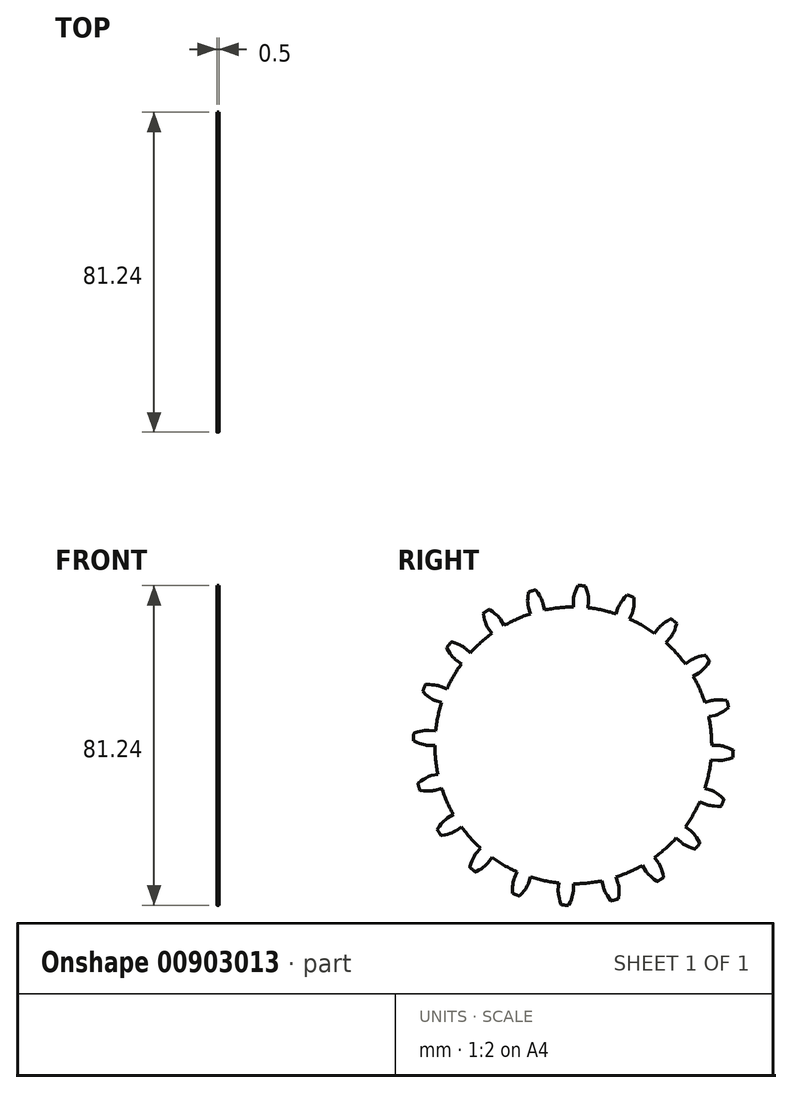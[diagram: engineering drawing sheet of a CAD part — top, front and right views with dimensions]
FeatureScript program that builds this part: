
annotation { "Feature Type Name" : "Feature", "Feature Type Description" : "" }
export const myFeature = defineFeature(function(context is Context, id is Id, definition is map)
    precondition{}
    {
        {
            assignVariable(context, id + "F0", {"name" : "GearThickness", "anyValue" : .5});
        }
        {
            var Q0;
            Q0=qCreatedBy(makeId("Right.planeOp"),FACE);
            var sketch = newSketch(context, id + "F1", { "sketchPlane" : qUnion([Q0])});
            skCircle(sketch, "E0", {"center": v(0, 0) * mm, "radius": 35.16 * mm});
            skCircle(sketch, "E1", {"center": v(0, 0) * mm, "radius": 36.89 * mm, "construction": true});
            skCircle(sketch, "E2", {"center": v(0, 0) * mm, "radius": 38.1 * mm, "construction": true});
            skCircle(sketch, "E3", {"center": v(0, 0) * mm, "radius": 40.64 * mm});
            skLineSegment(sketch, "E4", {"start": v(0, 0) * mm, "end": v(-36.89, 0) * mm, "construction": true});
            skLineSegment(sketch, "E5.1.0", {"start": v(0, 0) * mm, "end": v(-36.84, 1.84) * mm, "construction": true});
            skLineSegment(sketch, "E5.2.0", {"start": v(0, 0) * mm, "end": v(-36.7, 3.68) * mm, "construction": true});
            skLineSegment(sketch, "E5.3.0", {"start": v(0, 0) * mm, "end": v(-36.47, 5.51) * mm, "construction": true});
            skLineSegment(sketch, "E5.4.0", {"start": v(0, 0) * mm, "end": v(-36.15, 7.33) * mm, "construction": true});
            skLineSegment(sketch, "E5.5.0", {"start": v(0, 0) * mm, "end": v(-35.74, 9.13) * mm, "construction": true});
            skLineSegment(sketch, "E5.6.0", {"start": v(0, 0) * mm, "end": v(-35.24, 10.9) * mm, "construction": true});
            skLineSegment(sketch, "E5.7.0", {"start": v(0, 0) * mm, "end": v(-34.65, 12.65) * mm, "construction": true});
            skLineSegment(sketch, "E5.8.0", {"start": v(0, 0) * mm, "end": v(-33.97, 14.36) * mm, "construction": true});
            skLineSegment(sketch, "E5.9.0", {"start": v(0, 0) * mm, "end": v(-33.21, 16.04) * mm, "construction": true});
            skLineSegment(sketch, "E5.10.0", {"start": v(0, 0) * mm, "end": v(-32.37, 17.68) * mm, "construction": true});
            skLineSegment(sketch, "E5.11.0", {"start": v(0, 0) * mm, "end": v(-31.45, 19.28) * mm, "construction": true});
            skLineSegment(sketch, "E5.12.0", {"start": v(0, 0) * mm, "end": v(-30.44, 20.83) * mm, "construction": true});
            skLineSegment(sketch, "E5.13.0", {"start": v(0, 0) * mm, "end": v(-29.36, 22.32) * mm, "construction": true});
            skLineSegment(sketch, "E5.14.0", {"start": v(0, 0) * mm, "end": v(-28.21, 23.76) * mm, "construction": true});
            skLineSegment(sketch, "E5.anchor2", {"start": v(0, 0) * mm, "end": v(-28.21, 23.76) * mm, "construction": true});
            skLineSegment(sketch, "E6", {"start": v(-36.84, 1.84) * mm, "end": v(-36.93, 0) * mm, "construction": true});
            skLineSegment(sketch, "E7", {"start": v(-36.7, 3.68) * mm, "end": v(-37.07, 0.01) * mm, "construction": true});
            skLineSegment(sketch, "E8", {"start": v(-36.47, 5.51) * mm, "end": v(-37.3, 0.04) * mm, "construction": true});
            skLineSegment(sketch, "E9", {"start": v(-35.74, 9.13) * mm, "end": v(-38.02, 0.2) * mm, "construction": true});
            skLineSegment(sketch, "E10", {"start": v(-35.24, 10.9) * mm, "end": v(-38.5, 0.33) * mm, "construction": true});
            skLineSegment(sketch, "E11", {"start": v(-34.65, 12.65) * mm, "end": v(-39.08, 0.52) * mm, "construction": true});
            skLineSegment(sketch, "E12", {"start": v(-33.97, 14.36) * mm, "end": v(-39.72, 0.77) * mm, "construction": true});
            skLineSegment(sketch, "E13", {"start": v(-33.21, 16.04) * mm, "end": v(-40.43, 1.1) * mm, "construction": true});
            skLineSegment(sketch, "E14", {"start": v(-32.37, 17.68) * mm, "end": v(-41.21, 1.5) * mm, "construction": true});
            skLineSegment(sketch, "E15", {"start": v(-31.45, 19.28) * mm, "end": v(-42.05, 1.98) * mm, "construction": true});
            skLineSegment(sketch, "E16", {"start": v(-36.15, 7.33) * mm, "end": v(-37.62, 0.1) * mm, "construction": true});
            skLineSegment(sketch, "E17", {"start": v(-30.44, 20.83) * mm, "end": v(-42.94, 2.56) * mm, "construction": true});
            skLineSegment(sketch, "E18", {"start": v(-29.36, 22.32) * mm, "end": v(-43.87, 3.24) * mm, "construction": true});
            skLineSegment(sketch, "E19", {"start": v(-28.21, 23.76) * mm, "end": v(-44.85, 4.01) * mm, "construction": true});
            skLineSegment(sketch, "E20", {"start": v(0, 0) * mm, "end": v(-36.84, 1.93) * mm, "construction": true});
            skLineSegment(sketch, "E21", {"start": v(-35.16, 0) * mm, "end": v(-36.89, 0) * mm});
            skLineSegment(sketch, "E22.MirrorCS", {"start": v(-34.97, 3.68) * mm, "end": v(-36.68, 3.86) * mm});
            skLineSegment(sketch, "E23", {"start": v(-36.89, 0) * mm, "end": v(-36.93, 0) * mm});
            skLineSegment(sketch, "E24", {"start": v(-36.93, 0) * mm, "end": v(-37.07, 0.01) * mm});
            skLineSegment(sketch, "E25", {"start": v(-37.07, 0.01) * mm, "end": v(-37.3, 0.04) * mm});
            skLineSegment(sketch, "E26", {"start": v(-37.3, 0.04) * mm, "end": v(-37.62, 0.1) * mm});
            skLineSegment(sketch, "E27", {"start": v(-37.62, 0.1) * mm, "end": v(-38.02, 0.2) * mm});
            skLineSegment(sketch, "E28", {"start": v(-38.02, 0.2) * mm, "end": v(-38.5, 0.33) * mm});
            skLineSegment(sketch, "E29", {"start": v(-38.5, 0.33) * mm, "end": v(-39.08, 0.52) * mm});
            skLineSegment(sketch, "E30", {"start": v(-39.08, 0.52) * mm, "end": v(-39.72, 0.77) * mm});
            skLineSegment(sketch, "E31", {"start": v(-39.72, 0.77) * mm, "end": v(-40.43, 1.1) * mm});
            skLineSegment(sketch, "E32", {"start": v(-40.43, 1.1) * mm, "end": v(-41.21, 1.5) * mm});
            skLineSegment(sketch, "E33", {"start": v(-41.21, 1.5) * mm, "end": v(-42.05, 1.98) * mm});
            skLineSegment(sketch, "E34", {"start": v(-42.05, 1.98) * mm, "end": v(-42.94, 2.56) * mm});
            skLineSegment(sketch, "E35", {"start": v(-42.94, 2.56) * mm, "end": v(-43.87, 3.24) * mm});
            skLineSegment(sketch, "E36", {"start": v(-43.87, 3.24) * mm, "end": v(-44.85, 4.01) * mm});
            skLineSegment(sketch, "E37.MirrorCS", {"start": v(-36.68, 3.86) * mm, "end": v(-36.73, 3.86) * mm});
            skLineSegment(sketch, "E38.MirrorCS", {"start": v(-36.73, 3.86) * mm, "end": v(-36.87, 3.86) * mm});
            skLineSegment(sketch, "E39.MirrorCS", {"start": v(-36.87, 3.86) * mm, "end": v(-37.1, 3.86) * mm});
            skLineSegment(sketch, "E40.MirrorCS", {"start": v(-37.1, 3.86) * mm, "end": v(-37.42, 3.83) * mm});
            skLineSegment(sketch, "E41.MirrorCS", {"start": v(-37.83, 3.78) * mm, "end": v(-38.33, 3.7) * mm});
            skLineSegment(sketch, "E42.MirrorCS", {"start": v(-38.33, 3.7) * mm, "end": v(-38.92, 3.57) * mm});
            skLineSegment(sketch, "E43.MirrorCS", {"start": v(-38.92, 3.57) * mm, "end": v(-39.58, 3.38) * mm});
            skLineSegment(sketch, "E44.MirrorCS", {"start": v(-39.58, 3.38) * mm, "end": v(-40.33, 3.13) * mm});
            skLineSegment(sketch, "E45.MirrorCS", {"start": v(-41.14, 2.82) * mm, "end": v(-42.03, 2.42) * mm});
            skLineSegment(sketch, "E46.MirrorCS", {"start": v(-40.33, 3.13) * mm, "end": v(-41.14, 2.82) * mm});
            skLineSegment(sketch, "E47.MirrorCS", {"start": v(-42.03, 2.42) * mm, "end": v(-42.97, 1.94) * mm});
            skLineSegment(sketch, "E48.MirrorCS", {"start": v(-42.97, 1.94) * mm, "end": v(-43.97, 1.37) * mm});
            skLineSegment(sketch, "E49.MirrorCS", {"start": v(-43.97, 1.37) * mm, "end": v(-45.02, 0.7) * mm});
            skLineSegment(sketch, "E50.MirrorCS", {"start": v(-37.42, 3.83) * mm, "end": v(-37.83, 3.78) * mm});
            skLineSegment(sketch, "E51.1.0", {"start": v(-33.44, -10.87) * mm, "end": v(-35.08, -11.4) * mm});
            skLineSegment(sketch, "E51.1.1", {"start": v(-40.72, -10.68) * mm, "end": v(-41.47, -11.43) * mm});
            skLineSegment(sketch, "E51.1.2", {"start": v(-34.4, -7.31) * mm, "end": v(-36.08, -7.67) * mm});
            skLineSegment(sketch, "E51.1.3", {"start": v(-40, -10.03) * mm, "end": v(-40.72, -10.68) * mm});
            skLineSegment(sketch, "E51.1.4", {"start": v(-39.66, -11.31) * mm, "end": v(-40.6, -11.1) * mm});
            skLineSegment(sketch, "E51.1.5", {"start": v(-40.6, -11.1) * mm, "end": v(-41.63, -10.83) * mm});
            skLineSegment(sketch, "E51.1.6", {"start": v(-39.32, -9.48) * mm, "end": v(-40, -10.03) * mm});
            skLineSegment(sketch, "E51.1.7", {"start": v(-42.24, -12.29) * mm, "end": v(-43.03, -13.25) * mm});
            skLineSegment(sketch, "E51.1.8", {"start": v(-38.7, -9.02) * mm, "end": v(-39.32, -9.48) * mm});
            skLineSegment(sketch, "E51.1.9", {"start": v(-42.73, -10.48) * mm, "end": v(-43.9, -10.04) * mm});
            skLineSegment(sketch, "E51.1.10", {"start": v(-41.47, -11.43) * mm, "end": v(-42.24, -12.29) * mm});
            skLineSegment(sketch, "E51.1.11", {"start": v(-38.8, -11.45) * mm, "end": v(-39.66, -11.31) * mm});
            skLineSegment(sketch, "E51.1.12", {"start": v(-41.63, -10.83) * mm, "end": v(-42.73, -10.48) * mm});
            skLineSegment(sketch, "E51.1.13", {"start": v(-37.15, -8.1) * mm, "end": v(-37.6, -8.33) * mm});
            skLineSegment(sketch, "E51.1.14", {"start": v(-37.6, -8.33) * mm, "end": v(-38.11, -8.63) * mm});
            skLineSegment(sketch, "E51.1.15", {"start": v(-38.11, -8.63) * mm, "end": v(-38.7, -9.02) * mm});
            skLineSegment(sketch, "E51.1.16", {"start": v(-37.33, -11.58) * mm, "end": v(-38.02, -11.54) * mm});
            skLineSegment(sketch, "E51.1.17", {"start": v(-36.73, -11.59) * mm, "end": v(-37.33, -11.58) * mm});
            skLineSegment(sketch, "E51.1.18", {"start": v(-38.02, -11.54) * mm, "end": v(-38.8, -11.45) * mm});
            skLineSegment(sketch, "E51.1.19", {"start": v(-36.77, -7.92) * mm, "end": v(-37.15, -8.1) * mm});
            skLineSegment(sketch, "E51.1.20", {"start": v(-36.48, -7.8) * mm, "end": v(-36.77, -7.92) * mm});
            skLineSegment(sketch, "E51.1.21", {"start": v(-36.22, -11.57) * mm, "end": v(-36.73, -11.59) * mm});
            skLineSegment(sketch, "E51.1.22", {"start": v(-35.8, -11.53) * mm, "end": v(-36.22, -11.57) * mm});
            skLineSegment(sketch, "E51.1.23", {"start": v(-35.26, -11.44) * mm, "end": v(-35.49, -11.49) * mm});
            skLineSegment(sketch, "E51.1.24", {"start": v(-36.08, -7.67) * mm, "end": v(-36.13, -7.68) * mm});
            skLineSegment(sketch, "E51.1.25", {"start": v(-36.13, -7.68) * mm, "end": v(-36.26, -7.72) * mm});
            skLineSegment(sketch, "E51.1.26", {"start": v(-35.49, -11.49) * mm, "end": v(-35.8, -11.53) * mm});
            skLineSegment(sketch, "E51.1.27", {"start": v(-36.26, -7.72) * mm, "end": v(-36.48, -7.8) * mm});
            skLineSegment(sketch, "E51.1.28", {"start": v(-35.13, -11.41) * mm, "end": v(-35.26, -11.44) * mm});
            skLineSegment(sketch, "E51.1.29", {"start": v(-35.08, -11.4) * mm, "end": v(-35.13, -11.41) * mm});
            skLineSegment(sketch, "E51.2.0", {"start": v(-28.45, -20.67) * mm, "end": v(-29.84, -21.68) * mm});
            skLineSegment(sketch, "E51.2.1", {"start": v(-35.42, -22.74) * mm, "end": v(-35.9, -23.69) * mm});
            skLineSegment(sketch, "E51.2.2", {"start": v(-30.45, -17.58) * mm, "end": v(-31.94, -18.44) * mm});
            skLineSegment(sketch, "E51.2.3", {"start": v(-34.94, -21.9) * mm, "end": v(-35.42, -22.74) * mm});
            skLineSegment(sketch, "E51.2.4", {"start": v(-34.22, -23.01) * mm, "end": v(-35.19, -23.11) * mm});
            skLineSegment(sketch, "E51.2.5", {"start": v(-35.19, -23.11) * mm, "end": v(-36.24, -23.17) * mm});
            skLineSegment(sketch, "E51.2.6", {"start": v(-34.47, -21.17) * mm, "end": v(-34.94, -21.9) * mm});
            skLineSegment(sketch, "E51.2.7", {"start": v(-36.38, -24.74) * mm, "end": v(-36.83, -25.9) * mm});
            skLineSegment(sketch, "E51.2.8", {"start": v(-34.01, -20.53) * mm, "end": v(-34.47, -21.17) * mm});
            skLineSegment(sketch, "E51.2.9", {"start": v(-37.4, -23.17) * mm, "end": v(-38.64, -23.11) * mm});
            skLineSegment(sketch, "E51.2.10", {"start": v(-35.9, -23.69) * mm, "end": v(-36.38, -24.74) * mm});
            skLineSegment(sketch, "E51.2.11", {"start": v(-33.36, -22.88) * mm, "end": v(-34.22, -23.01) * mm});
            skLineSegment(sketch, "E51.2.12", {"start": v(-36.24, -23.17) * mm, "end": v(-37.4, -23.17) * mm});
            skLineSegment(sketch, "E51.2.13", {"start": v(-32.83, -19.18) * mm, "end": v(-33.19, -19.54) * mm});
            skLineSegment(sketch, "E51.2.14", {"start": v(-33.19, -19.54) * mm, "end": v(-33.58, -19.99) * mm});
            skLineSegment(sketch, "E51.2.15", {"start": v(-33.58, -19.99) * mm, "end": v(-34.01, -20.53) * mm});
            skLineSegment(sketch, "E51.2.16", {"start": v(-31.92, -22.55) * mm, "end": v(-32.59, -22.72) * mm});
            skLineSegment(sketch, "E51.2.17", {"start": v(-31.35, -22.37) * mm, "end": v(-31.92, -22.55) * mm});
            skLineSegment(sketch, "E51.2.18", {"start": v(-32.59, -22.72) * mm, "end": v(-33.36, -22.88) * mm});
            skLineSegment(sketch, "E51.2.19", {"start": v(-32.53, -18.9) * mm, "end": v(-32.83, -19.18) * mm});
            skLineSegment(sketch, "E51.2.20", {"start": v(-32.28, -18.69) * mm, "end": v(-32.53, -18.9) * mm});
            skLineSegment(sketch, "E51.2.21", {"start": v(-30.87, -22.2) * mm, "end": v(-31.35, -22.37) * mm});
            skLineSegment(sketch, "E51.2.22", {"start": v(-30.5, -22.03) * mm, "end": v(-30.87, -22.2) * mm});
            skLineSegment(sketch, "E51.2.23", {"start": v(-30, -21.78) * mm, "end": v(-30.2, -21.9) * mm});
            skLineSegment(sketch, "E51.2.24", {"start": v(-31.94, -18.44) * mm, "end": v(-31.98, -18.47) * mm});
            skLineSegment(sketch, "E51.2.25", {"start": v(-31.98, -18.47) * mm, "end": v(-32.1, -18.55) * mm});
            skLineSegment(sketch, "E51.2.26", {"start": v(-30.2, -21.9) * mm, "end": v(-30.5, -22.03) * mm});
            skLineSegment(sketch, "E51.2.27", {"start": v(-32.1, -18.55) * mm, "end": v(-32.28, -18.69) * mm});
            skLineSegment(sketch, "E51.2.28", {"start": v(-29.88, -21.7) * mm, "end": v(-30, -21.78) * mm});
            skLineSegment(sketch, "E51.2.29", {"start": v(-29.84, -21.68) * mm, "end": v(-29.88, -21.7) * mm});
            skLineSegment(sketch, "E51.3.0", {"start": v(-20.67, -28.45) * mm, "end": v(-21.68, -29.84) * mm});
            skLineSegment(sketch, "E51.3.1", {"start": v(-26.66, -32.58) * mm, "end": v(-26.83, -33.62) * mm});
            skLineSegment(sketch, "E51.3.2", {"start": v(-23.53, -26.13) * mm, "end": v(-24.68, -27.41) * mm});
            skLineSegment(sketch, "E51.3.3", {"start": v(-26.46, -31.63) * mm, "end": v(-26.66, -32.58) * mm});
            skLineSegment(sketch, "E51.3.4", {"start": v(-25.44, -32.46) * mm, "end": v(-26.32, -32.85) * mm});
            skLineSegment(sketch, "E51.3.5", {"start": v(-26.32, -32.85) * mm, "end": v(-27.31, -33.23) * mm});
            skLineSegment(sketch, "E51.3.6", {"start": v(-26.24, -30.78) * mm, "end": v(-26.46, -31.63) * mm});
            skLineSegment(sketch, "E51.3.7", {"start": v(-26.95, -34.77) * mm, "end": v(-27.02, -36.01) * mm});
            skLineSegment(sketch, "E51.3.8", {"start": v(-26, -30.04) * mm, "end": v(-26.24, -30.78) * mm});
            skLineSegment(sketch, "E51.3.9", {"start": v(-28.4, -33.6) * mm, "end": v(-29.6, -33.92) * mm});
            skLineSegment(sketch, "E51.3.10", {"start": v(-26.83, -33.62) * mm, "end": v(-26.95, -34.77) * mm});
            skLineSegment(sketch, "E51.3.11", {"start": v(-24.65, -32.07) * mm, "end": v(-25.44, -32.46) * mm});
            skLineSegment(sketch, "E51.3.12", {"start": v(-27.31, -33.23) * mm, "end": v(-28.4, -33.6) * mm});
            skLineSegment(sketch, "E51.3.13", {"start": v(-25.3, -28.38) * mm, "end": v(-25.52, -28.84) * mm});
            skLineSegment(sketch, "E51.3.14", {"start": v(-25.52, -28.84) * mm, "end": v(-25.76, -29.39) * mm});
            skLineSegment(sketch, "E51.3.15", {"start": v(-25.76, -29.39) * mm, "end": v(-26, -30.04) * mm});
            skLineSegment(sketch, "E51.3.16", {"start": v(-23.4, -31.3) * mm, "end": v(-23.97, -31.68) * mm});
            skLineSegment(sketch, "E51.3.17", {"start": v(-22.9, -30.96) * mm, "end": v(-23.4, -31.3) * mm});
            skLineSegment(sketch, "E51.3.18", {"start": v(-23.97, -31.68) * mm, "end": v(-24.65, -32.07) * mm});
            skLineSegment(sketch, "E51.3.19", {"start": v(-25.1, -28.02) * mm, "end": v(-25.3, -28.38) * mm});
            skLineSegment(sketch, "E51.3.20", {"start": v(-24.93, -27.75) * mm, "end": v(-25.1, -28.02) * mm});
            skLineSegment(sketch, "E51.3.21", {"start": v(-22.5, -30.65) * mm, "end": v(-22.9, -30.96) * mm});
            skLineSegment(sketch, "E51.3.22", {"start": v(-22.19, -30.38) * mm, "end": v(-22.5, -30.65) * mm});
            skLineSegment(sketch, "E51.3.23", {"start": v(-21.8, -29.98) * mm, "end": v(-21.96, -30.15) * mm});
            skLineSegment(sketch, "E51.3.24", {"start": v(-24.68, -27.41) * mm, "end": v(-24.71, -27.45) * mm});
            skLineSegment(sketch, "E51.3.25", {"start": v(-24.71, -27.45) * mm, "end": v(-24.8, -27.56) * mm});
            skLineSegment(sketch, "E51.3.26", {"start": v(-21.96, -30.15) * mm, "end": v(-22.19, -30.38) * mm});
            skLineSegment(sketch, "E51.3.27", {"start": v(-24.8, -27.56) * mm, "end": v(-24.93, -27.75) * mm});
            skLineSegment(sketch, "E51.3.28", {"start": v(-21.7, -29.88) * mm, "end": v(-21.8, -29.98) * mm});
            skLineSegment(sketch, "E51.3.29", {"start": v(-21.68, -29.84) * mm, "end": v(-21.7, -29.88) * mm});
            skLineSegment(sketch, "E51.4.0", {"start": v(-10.87, -33.44) * mm, "end": v(-11.4, -35.08) * mm});
            skLineSegment(sketch, "E51.4.1", {"start": v(-15.3, -39.22) * mm, "end": v(-15.13, -40.27) * mm});
            skLineSegment(sketch, "E51.4.2", {"start": v(-14.3, -32.12) * mm, "end": v(-15, -33.7) * mm});
            skLineSegment(sketch, "E51.4.3", {"start": v(-15.4, -38.26) * mm, "end": v(-15.3, -39.22) * mm});
            skLineSegment(sketch, "E51.4.4", {"start": v(-14.16, -38.73) * mm, "end": v(-14.88, -39.38) * mm});
            skLineSegment(sketch, "E51.4.5", {"start": v(-14.88, -39.38) * mm, "end": v(-15.7, -40.05) * mm});
            skLineSegment(sketch, "E51.4.6", {"start": v(-15.44, -37.39) * mm, "end": v(-15.4, -38.26) * mm});
            skLineSegment(sketch, "E51.4.7", {"start": v(-14.89, -41.4) * mm, "end": v(-14.57, -42.6) * mm});
            skLineSegment(sketch, "E51.4.8", {"start": v(-15.45, -36.6) * mm, "end": v(-15.44, -37.39) * mm});
            skLineSegment(sketch, "E51.4.9", {"start": v(-16.64, -40.73) * mm, "end": v(-17.68, -41.41) * mm});
            skLineSegment(sketch, "E51.4.10", {"start": v(-15.13, -40.27) * mm, "end": v(-14.89, -41.4) * mm});
            skLineSegment(sketch, "E51.4.11", {"start": v(-13.54, -38.12) * mm, "end": v(-14.16, -38.73) * mm});
            skLineSegment(sketch, "E51.4.12", {"start": v(-15.7, -40.05) * mm, "end": v(-16.64, -40.73) * mm});
            skLineSegment(sketch, "E51.4.13", {"start": v(-15.3, -34.81) * mm, "end": v(-15.36, -35.31) * mm});
            skLineSegment(sketch, "E51.4.14", {"start": v(-15.36, -35.31) * mm, "end": v(-15.42, -35.91) * mm});
            skLineSegment(sketch, "E51.4.15", {"start": v(-15.42, -35.91) * mm, "end": v(-15.45, -36.6) * mm});
            skLineSegment(sketch, "E51.4.16", {"start": v(-12.57, -37) * mm, "end": v(-13.01, -37.54) * mm});
            skLineSegment(sketch, "E51.4.17", {"start": v(-12.21, -36.52) * mm, "end": v(-12.57, -37) * mm});
            skLineSegment(sketch, "E51.4.18", {"start": v(-13.01, -37.54) * mm, "end": v(-13.54, -38.12) * mm});
            skLineSegment(sketch, "E51.4.19", {"start": v(-15.21, -34.4) * mm, "end": v(-15.3, -34.81) * mm});
            skLineSegment(sketch, "E51.4.20", {"start": v(-15.13, -34.1) * mm, "end": v(-15.21, -34.4) * mm});
            skLineSegment(sketch, "E51.4.21", {"start": v(-11.93, -36.1) * mm, "end": v(-12.21, -36.52) * mm});
            skLineSegment(sketch, "E51.4.22", {"start": v(-11.72, -35.75) * mm, "end": v(-11.93, -36.1) * mm});
            skLineSegment(sketch, "E51.4.23", {"start": v(-11.47, -35.25) * mm, "end": v(-11.57, -35.46) * mm});
            skLineSegment(sketch, "E51.4.24", {"start": v(-15, -33.7) * mm, "end": v(-15.02, -33.74) * mm});
            skLineSegment(sketch, "E51.4.25", {"start": v(-15.02, -33.74) * mm, "end": v(-15.07, -33.87) * mm});
            skLineSegment(sketch, "E51.4.26", {"start": v(-11.57, -35.46) * mm, "end": v(-11.72, -35.75) * mm});
            skLineSegment(sketch, "E51.4.27", {"start": v(-15.07, -33.87) * mm, "end": v(-15.13, -34.1) * mm});
            skLineSegment(sketch, "E51.4.28", {"start": v(-11.41, -35.12) * mm, "end": v(-11.47, -35.25) * mm});
            skLineSegment(sketch, "E51.4.29", {"start": v(-11.4, -35.08) * mm, "end": v(-11.41, -35.12) * mm});
            skLineSegment(sketch, "E51.5.0", {"start": v(0, -35.16) * mm, "end": v(0, -36.89) * mm});
            skLineSegment(sketch, "E51.5.1", {"start": v(-2.42, -42.03) * mm, "end": v(-1.94, -42.97) * mm});
            skLineSegment(sketch, "E51.5.2", {"start": v(-3.68, -34.97) * mm, "end": v(-3.86, -36.68) * mm});
            skLineSegment(sketch, "E51.5.3", {"start": v(-2.82, -41.14) * mm, "end": v(-2.42, -42.03) * mm});
            skLineSegment(sketch, "E51.5.4", {"start": v(-1.5, -41.21) * mm, "end": v(-1.98, -42.05) * mm});
            skLineSegment(sketch, "E51.5.5", {"start": v(-1.98, -42.05) * mm, "end": v(-2.56, -42.94) * mm});
            skLineSegment(sketch, "E51.5.6", {"start": v(-3.13, -40.33) * mm, "end": v(-2.82, -41.14) * mm});
            skLineSegment(sketch, "E51.5.7", {"start": v(-1.37, -43.97) * mm, "end": v(-0.7, -45.02) * mm});
            skLineSegment(sketch, "E51.5.8", {"start": v(-3.38, -39.58) * mm, "end": v(-3.13, -40.33) * mm});
            skLineSegment(sketch, "E51.5.9", {"start": v(-3.24, -43.87) * mm, "end": v(-4.01, -44.85) * mm});
            skLineSegment(sketch, "E51.5.10", {"start": v(-1.94, -42.97) * mm, "end": v(-1.37, -43.97) * mm});
            skLineSegment(sketch, "E51.5.11", {"start": v(-1.1, -40.43) * mm, "end": v(-1.5, -41.21) * mm});
            skLineSegment(sketch, "E51.5.12", {"start": v(-2.56, -42.94) * mm, "end": v(-3.24, -43.87) * mm});
            skLineSegment(sketch, "E51.5.13", {"start": v(-3.78, -37.83) * mm, "end": v(-3.7, -38.33) * mm});
            skLineSegment(sketch, "E51.5.14", {"start": v(-3.7, -38.33) * mm, "end": v(-3.57, -38.92) * mm});
            skLineSegment(sketch, "E51.5.15", {"start": v(-3.57, -38.92) * mm, "end": v(-3.38, -39.58) * mm});
            skLineSegment(sketch, "E51.5.16", {"start": v(-0.52, -39.08) * mm, "end": v(-0.77, -39.72) * mm});
            skLineSegment(sketch, "E51.5.17", {"start": v(-0.33, -38.5) * mm, "end": v(-0.52, -39.08) * mm});
            skLineSegment(sketch, "E51.5.18", {"start": v(-0.77, -39.72) * mm, "end": v(-1.1, -40.43) * mm});
            skLineSegment(sketch, "E51.5.19", {"start": v(-3.83, -37.42) * mm, "end": v(-3.78, -37.83) * mm});
            skLineSegment(sketch, "E51.5.20", {"start": v(-3.86, -37.1) * mm, "end": v(-3.83, -37.42) * mm});
            skLineSegment(sketch, "E51.5.21", {"start": v(-0.2, -38.02) * mm, "end": v(-0.33, -38.5) * mm});
            skLineSegment(sketch, "E51.5.22", {"start": v(-0.1, -37.62) * mm, "end": v(-0.2, -38.02) * mm});
            skLineSegment(sketch, "E51.5.23", {"start": v(-0.01, -37.07) * mm, "end": v(-0.04, -37.3) * mm});
            skLineSegment(sketch, "E51.5.24", {"start": v(-3.86, -36.68) * mm, "end": v(-3.86, -36.73) * mm});
            skLineSegment(sketch, "E51.5.25", {"start": v(-3.86, -36.73) * mm, "end": v(-3.86, -36.87) * mm});
            skLineSegment(sketch, "E51.5.26", {"start": v(-0.04, -37.3) * mm, "end": v(-0.1, -37.62) * mm});
            skLineSegment(sketch, "E51.5.27", {"start": v(-3.86, -36.87) * mm, "end": v(-3.86, -37.1) * mm});
            skLineSegment(sketch, "E51.5.28", {"start": v(0, -36.93) * mm, "end": v(-0.01, -37.07) * mm});
            skLineSegment(sketch, "E51.5.29", {"start": v(0, -36.89) * mm, "end": v(0, -36.93) * mm});
            skLineSegment(sketch, "E51.6.0", {"start": v(10.87, -33.44) * mm, "end": v(11.4, -35.08) * mm});
            skLineSegment(sketch, "E51.6.1", {"start": v(10.68, -40.72) * mm, "end": v(11.43, -41.47) * mm});
            skLineSegment(sketch, "E51.6.2", {"start": v(7.31, -34.4) * mm, "end": v(7.67, -36.08) * mm});
            skLineSegment(sketch, "E51.6.3", {"start": v(10.03, -40) * mm, "end": v(10.68, -40.72) * mm});
            skLineSegment(sketch, "E51.6.4", {"start": v(11.31, -39.66) * mm, "end": v(11.1, -40.6) * mm});
            skLineSegment(sketch, "E51.6.5", {"start": v(11.1, -40.6) * mm, "end": v(10.83, -41.63) * mm});
            skLineSegment(sketch, "E51.6.6", {"start": v(9.48, -39.32) * mm, "end": v(10.03, -40) * mm});
            skLineSegment(sketch, "E51.6.7", {"start": v(12.29, -42.24) * mm, "end": v(13.25, -43.03) * mm});
            skLineSegment(sketch, "E51.6.8", {"start": v(9.02, -38.7) * mm, "end": v(9.48, -39.32) * mm});
            skLineSegment(sketch, "E51.6.9", {"start": v(10.48, -42.73) * mm, "end": v(10.04, -43.9) * mm});
            skLineSegment(sketch, "E51.6.10", {"start": v(11.43, -41.47) * mm, "end": v(12.29, -42.24) * mm});
            skLineSegment(sketch, "E51.6.11", {"start": v(11.45, -38.8) * mm, "end": v(11.31, -39.66) * mm});
            skLineSegment(sketch, "E51.6.12", {"start": v(10.83, -41.63) * mm, "end": v(10.48, -42.73) * mm});
            skLineSegment(sketch, "E51.6.13", {"start": v(8.1, -37.15) * mm, "end": v(8.33, -37.6) * mm});
            skLineSegment(sketch, "E51.6.14", {"start": v(8.33, -37.6) * mm, "end": v(8.63, -38.11) * mm});
            skLineSegment(sketch, "E51.6.15", {"start": v(8.63, -38.11) * mm, "end": v(9.02, -38.7) * mm});
            skLineSegment(sketch, "E51.6.16", {"start": v(11.58, -37.33) * mm, "end": v(11.54, -38.02) * mm});
            skLineSegment(sketch, "E51.6.17", {"start": v(11.59, -36.73) * mm, "end": v(11.58, -37.33) * mm});
            skLineSegment(sketch, "E51.6.18", {"start": v(11.54, -38.02) * mm, "end": v(11.45, -38.8) * mm});
            skLineSegment(sketch, "E51.6.19", {"start": v(7.92, -36.77) * mm, "end": v(8.1, -37.15) * mm});
            skLineSegment(sketch, "E51.6.20", {"start": v(7.8, -36.48) * mm, "end": v(7.92, -36.77) * mm});
            skLineSegment(sketch, "E51.6.21", {"start": v(11.57, -36.22) * mm, "end": v(11.59, -36.73) * mm});
            skLineSegment(sketch, "E51.6.22", {"start": v(11.53, -35.8) * mm, "end": v(11.57, -36.22) * mm});
            skLineSegment(sketch, "E51.6.23", {"start": v(11.44, -35.26) * mm, "end": v(11.49, -35.49) * mm});
            skLineSegment(sketch, "E51.6.24", {"start": v(7.67, -36.08) * mm, "end": v(7.68, -36.13) * mm});
            skLineSegment(sketch, "E51.6.25", {"start": v(7.68, -36.13) * mm, "end": v(7.72, -36.26) * mm});
            skLineSegment(sketch, "E51.6.26", {"start": v(11.49, -35.49) * mm, "end": v(11.53, -35.8) * mm});
            skLineSegment(sketch, "E51.6.27", {"start": v(7.72, -36.26) * mm, "end": v(7.8, -36.48) * mm});
            skLineSegment(sketch, "E51.6.28", {"start": v(11.41, -35.13) * mm, "end": v(11.44, -35.26) * mm});
            skLineSegment(sketch, "E51.6.29", {"start": v(11.4, -35.08) * mm, "end": v(11.41, -35.13) * mm});
            skLineSegment(sketch, "E51.7.0", {"start": v(20.67, -28.45) * mm, "end": v(21.68, -29.84) * mm});
            skLineSegment(sketch, "E51.7.1", {"start": v(22.74, -35.42) * mm, "end": v(23.69, -35.9) * mm});
            skLineSegment(sketch, "E51.7.2", {"start": v(17.58, -30.45) * mm, "end": v(18.44, -31.94) * mm});
            skLineSegment(sketch, "E51.7.3", {"start": v(21.9, -34.94) * mm, "end": v(22.74, -35.42) * mm});
            skLineSegment(sketch, "E51.7.4", {"start": v(23.01, -34.22) * mm, "end": v(23.11, -35.19) * mm});
            skLineSegment(sketch, "E51.7.5", {"start": v(23.11, -35.19) * mm, "end": v(23.17, -36.24) * mm});
            skLineSegment(sketch, "E51.7.6", {"start": v(21.17, -34.47) * mm, "end": v(21.9, -34.94) * mm});
            skLineSegment(sketch, "E51.7.7", {"start": v(24.74, -36.38) * mm, "end": v(25.9, -36.83) * mm});
            skLineSegment(sketch, "E51.7.8", {"start": v(20.53, -34.01) * mm, "end": v(21.17, -34.47) * mm});
            skLineSegment(sketch, "E51.7.9", {"start": v(23.17, -37.4) * mm, "end": v(23.11, -38.64) * mm});
            skLineSegment(sketch, "E51.7.10", {"start": v(23.69, -35.9) * mm, "end": v(24.74, -36.38) * mm});
            skLineSegment(sketch, "E51.7.11", {"start": v(22.88, -33.36) * mm, "end": v(23.01, -34.22) * mm});
            skLineSegment(sketch, "E51.7.12", {"start": v(23.17, -36.24) * mm, "end": v(23.17, -37.4) * mm});
            skLineSegment(sketch, "E51.7.13", {"start": v(19.18, -32.83) * mm, "end": v(19.54, -33.19) * mm});
            skLineSegment(sketch, "E51.7.14", {"start": v(19.54, -33.19) * mm, "end": v(19.99, -33.58) * mm});
            skLineSegment(sketch, "E51.7.15", {"start": v(19.99, -33.58) * mm, "end": v(20.53, -34.01) * mm});
            skLineSegment(sketch, "E51.7.16", {"start": v(22.55, -31.92) * mm, "end": v(22.72, -32.59) * mm});
            skLineSegment(sketch, "E51.7.17", {"start": v(22.37, -31.35) * mm, "end": v(22.55, -31.92) * mm});
            skLineSegment(sketch, "E51.7.18", {"start": v(22.72, -32.59) * mm, "end": v(22.88, -33.36) * mm});
            skLineSegment(sketch, "E51.7.19", {"start": v(18.9, -32.53) * mm, "end": v(19.18, -32.83) * mm});
            skLineSegment(sketch, "E51.7.20", {"start": v(18.69, -32.28) * mm, "end": v(18.9, -32.53) * mm});
            skLineSegment(sketch, "E51.7.21", {"start": v(22.2, -30.87) * mm, "end": v(22.37, -31.35) * mm});
            skLineSegment(sketch, "E51.7.22", {"start": v(22.03, -30.5) * mm, "end": v(22.2, -30.87) * mm});
            skLineSegment(sketch, "E51.7.23", {"start": v(21.78, -30) * mm, "end": v(21.9, -30.2) * mm});
            skLineSegment(sketch, "E51.7.24", {"start": v(18.44, -31.94) * mm, "end": v(18.47, -31.98) * mm});
            skLineSegment(sketch, "E51.7.25", {"start": v(18.47, -31.98) * mm, "end": v(18.55, -32.1) * mm});
            skLineSegment(sketch, "E51.7.26", {"start": v(21.9, -30.2) * mm, "end": v(22.03, -30.5) * mm});
            skLineSegment(sketch, "E51.7.27", {"start": v(18.55, -32.1) * mm, "end": v(18.69, -32.28) * mm});
            skLineSegment(sketch, "E51.7.28", {"start": v(21.7, -29.88) * mm, "end": v(21.78, -30) * mm});
            skLineSegment(sketch, "E51.7.29", {"start": v(21.68, -29.84) * mm, "end": v(21.7, -29.88) * mm});
            skLineSegment(sketch, "E51.8.0", {"start": v(28.45, -20.67) * mm, "end": v(29.84, -21.68) * mm});
            skLineSegment(sketch, "E51.8.1", {"start": v(32.58, -26.66) * mm, "end": v(33.62, -26.83) * mm});
            skLineSegment(sketch, "E51.8.2", {"start": v(26.13, -23.53) * mm, "end": v(27.41, -24.68) * mm});
            skLineSegment(sketch, "E51.8.3", {"start": v(31.63, -26.46) * mm, "end": v(32.58, -26.66) * mm});
            skLineSegment(sketch, "E51.8.4", {"start": v(32.46, -25.44) * mm, "end": v(32.85, -26.32) * mm});
            skLineSegment(sketch, "E51.8.5", {"start": v(32.85, -26.32) * mm, "end": v(33.23, -27.31) * mm});
            skLineSegment(sketch, "E51.8.6", {"start": v(30.78, -26.24) * mm, "end": v(31.63, -26.46) * mm});
            skLineSegment(sketch, "E51.8.7", {"start": v(34.77, -26.95) * mm, "end": v(36.01, -27.02) * mm});
            skLineSegment(sketch, "E51.8.8", {"start": v(30.04, -26) * mm, "end": v(30.78, -26.24) * mm});
            skLineSegment(sketch, "E51.8.9", {"start": v(33.6, -28.4) * mm, "end": v(33.92, -29.6) * mm});
            skLineSegment(sketch, "E51.8.10", {"start": v(33.62, -26.83) * mm, "end": v(34.77, -26.95) * mm});
            skLineSegment(sketch, "E51.8.11", {"start": v(32.07, -24.65) * mm, "end": v(32.46, -25.44) * mm});
            skLineSegment(sketch, "E51.8.12", {"start": v(33.23, -27.31) * mm, "end": v(33.6, -28.4) * mm});
            skLineSegment(sketch, "E51.8.13", {"start": v(28.38, -25.3) * mm, "end": v(28.84, -25.52) * mm});
            skLineSegment(sketch, "E51.8.14", {"start": v(28.84, -25.52) * mm, "end": v(29.39, -25.76) * mm});
            skLineSegment(sketch, "E51.8.15", {"start": v(29.39, -25.76) * mm, "end": v(30.04, -26) * mm});
            skLineSegment(sketch, "E51.8.16", {"start": v(31.3, -23.4) * mm, "end": v(31.68, -23.97) * mm});
            skLineSegment(sketch, "E51.8.17", {"start": v(30.96, -22.9) * mm, "end": v(31.3, -23.4) * mm});
            skLineSegment(sketch, "E51.8.18", {"start": v(31.68, -23.97) * mm, "end": v(32.07, -24.65) * mm});
            skLineSegment(sketch, "E51.8.19", {"start": v(28.02, -25.1) * mm, "end": v(28.38, -25.3) * mm});
            skLineSegment(sketch, "E51.8.20", {"start": v(27.75, -24.93) * mm, "end": v(28.02, -25.1) * mm});
            skLineSegment(sketch, "E51.8.21", {"start": v(30.65, -22.5) * mm, "end": v(30.96, -22.9) * mm});
            skLineSegment(sketch, "E51.8.22", {"start": v(30.38, -22.19) * mm, "end": v(30.65, -22.5) * mm});
            skLineSegment(sketch, "E51.8.23", {"start": v(29.98, -21.8) * mm, "end": v(30.15, -21.96) * mm});
            skLineSegment(sketch, "E51.8.24", {"start": v(27.41, -24.68) * mm, "end": v(27.45, -24.71) * mm});
            skLineSegment(sketch, "E51.8.25", {"start": v(27.45, -24.71) * mm, "end": v(27.56, -24.8) * mm});
            skLineSegment(sketch, "E51.8.26", {"start": v(30.15, -21.96) * mm, "end": v(30.38, -22.19) * mm});
            skLineSegment(sketch, "E51.8.27", {"start": v(27.56, -24.8) * mm, "end": v(27.75, -24.93) * mm});
            skLineSegment(sketch, "E51.8.28", {"start": v(29.88, -21.7) * mm, "end": v(29.98, -21.8) * mm});
            skLineSegment(sketch, "E51.8.29", {"start": v(29.84, -21.68) * mm, "end": v(29.88, -21.7) * mm});
            skLineSegment(sketch, "E51.9.0", {"start": v(33.44, -10.87) * mm, "end": v(35.08, -11.4) * mm});
            skLineSegment(sketch, "E51.9.1", {"start": v(39.22, -15.3) * mm, "end": v(40.27, -15.13) * mm});
            skLineSegment(sketch, "E51.9.2", {"start": v(32.12, -14.3) * mm, "end": v(33.7, -15) * mm});
            skLineSegment(sketch, "E51.9.3", {"start": v(38.26, -15.4) * mm, "end": v(39.22, -15.3) * mm});
            skLineSegment(sketch, "E51.9.4", {"start": v(38.73, -14.16) * mm, "end": v(39.38, -14.88) * mm});
            skLineSegment(sketch, "E51.9.5", {"start": v(39.38, -14.88) * mm, "end": v(40.05, -15.7) * mm});
            skLineSegment(sketch, "E51.9.6", {"start": v(37.39, -15.44) * mm, "end": v(38.26, -15.4) * mm});
            skLineSegment(sketch, "E51.9.7", {"start": v(41.4, -14.89) * mm, "end": v(42.6, -14.57) * mm});
            skLineSegment(sketch, "E51.9.8", {"start": v(36.6, -15.45) * mm, "end": v(37.39, -15.44) * mm});
            skLineSegment(sketch, "E51.9.9", {"start": v(40.73, -16.64) * mm, "end": v(41.41, -17.68) * mm});
            skLineSegment(sketch, "E51.9.10", {"start": v(40.27, -15.13) * mm, "end": v(41.4, -14.89) * mm});
            skLineSegment(sketch, "E51.9.11", {"start": v(38.12, -13.54) * mm, "end": v(38.73, -14.16) * mm});
            skLineSegment(sketch, "E51.9.12", {"start": v(40.05, -15.7) * mm, "end": v(40.73, -16.64) * mm});
            skLineSegment(sketch, "E51.9.13", {"start": v(34.81, -15.3) * mm, "end": v(35.31, -15.36) * mm});
            skLineSegment(sketch, "E51.9.14", {"start": v(35.31, -15.36) * mm, "end": v(35.91, -15.42) * mm});
            skLineSegment(sketch, "E51.9.15", {"start": v(35.91, -15.42) * mm, "end": v(36.6, -15.45) * mm});
            skLineSegment(sketch, "E51.9.16", {"start": v(37, -12.57) * mm, "end": v(37.54, -13.01) * mm});
            skLineSegment(sketch, "E51.9.17", {"start": v(36.52, -12.21) * mm, "end": v(37, -12.57) * mm});
            skLineSegment(sketch, "E51.9.18", {"start": v(37.54, -13.01) * mm, "end": v(38.12, -13.54) * mm});
            skLineSegment(sketch, "E51.9.19", {"start": v(34.4, -15.21) * mm, "end": v(34.81, -15.3) * mm});
            skLineSegment(sketch, "E51.9.20", {"start": v(34.1, -15.13) * mm, "end": v(34.4, -15.21) * mm});
            skLineSegment(sketch, "E51.9.21", {"start": v(36.1, -11.93) * mm, "end": v(36.52, -12.21) * mm});
            skLineSegment(sketch, "E51.9.22", {"start": v(35.75, -11.72) * mm, "end": v(36.1, -11.93) * mm});
            skLineSegment(sketch, "E51.9.23", {"start": v(35.25, -11.47) * mm, "end": v(35.46, -11.57) * mm});
            skLineSegment(sketch, "E51.9.24", {"start": v(33.7, -15) * mm, "end": v(33.74, -15.02) * mm});
            skLineSegment(sketch, "E51.9.25", {"start": v(33.74, -15.02) * mm, "end": v(33.87, -15.07) * mm});
            skLineSegment(sketch, "E51.9.26", {"start": v(35.46, -11.57) * mm, "end": v(35.75, -11.72) * mm});
            skLineSegment(sketch, "E51.9.27", {"start": v(33.87, -15.07) * mm, "end": v(34.1, -15.13) * mm});
            skLineSegment(sketch, "E51.9.28", {"start": v(35.12, -11.41) * mm, "end": v(35.25, -11.47) * mm});
            skLineSegment(sketch, "E51.9.29", {"start": v(35.08, -11.4) * mm, "end": v(35.12, -11.41) * mm});
            skLineSegment(sketch, "E51.10.0", {"start": v(35.16, 0) * mm, "end": v(36.89, 0) * mm});
            skLineSegment(sketch, "E51.10.1", {"start": v(42.03, -2.42) * mm, "end": v(42.97, -1.94) * mm});
            skLineSegment(sketch, "E51.10.2", {"start": v(34.97, -3.68) * mm, "end": v(36.68, -3.86) * mm});
            skLineSegment(sketch, "E51.10.3", {"start": v(41.14, -2.82) * mm, "end": v(42.03, -2.42) * mm});
            skLineSegment(sketch, "E51.10.4", {"start": v(41.21, -1.5) * mm, "end": v(42.05, -1.98) * mm});
            skLineSegment(sketch, "E51.10.5", {"start": v(42.05, -1.98) * mm, "end": v(42.94, -2.56) * mm});
            skLineSegment(sketch, "E51.10.6", {"start": v(40.33, -3.13) * mm, "end": v(41.14, -2.82) * mm});
            skLineSegment(sketch, "E51.10.7", {"start": v(43.97, -1.37) * mm, "end": v(45.02, -0.7) * mm});
            skLineSegment(sketch, "E51.10.8", {"start": v(39.58, -3.38) * mm, "end": v(40.33, -3.13) * mm});
            skLineSegment(sketch, "E51.10.9", {"start": v(43.87, -3.24) * mm, "end": v(44.85, -4.01) * mm});
            skLineSegment(sketch, "E51.10.10", {"start": v(42.97, -1.94) * mm, "end": v(43.97, -1.37) * mm});
            skLineSegment(sketch, "E51.10.11", {"start": v(40.43, -1.1) * mm, "end": v(41.21, -1.5) * mm});
            skLineSegment(sketch, "E51.10.12", {"start": v(42.94, -2.56) * mm, "end": v(43.87, -3.24) * mm});
            skLineSegment(sketch, "E51.10.13", {"start": v(37.83, -3.78) * mm, "end": v(38.33, -3.7) * mm});
            skLineSegment(sketch, "E51.10.14", {"start": v(38.33, -3.7) * mm, "end": v(38.92, -3.57) * mm});
            skLineSegment(sketch, "E51.10.15", {"start": v(38.92, -3.57) * mm, "end": v(39.58, -3.38) * mm});
            skLineSegment(sketch, "E51.10.16", {"start": v(39.08, -0.52) * mm, "end": v(39.72, -0.77) * mm});
            skLineSegment(sketch, "E51.10.17", {"start": v(38.5, -0.33) * mm, "end": v(39.08, -0.52) * mm});
            skLineSegment(sketch, "E51.10.18", {"start": v(39.72, -0.77) * mm, "end": v(40.43, -1.1) * mm});
            skLineSegment(sketch, "E51.10.19", {"start": v(37.42, -3.83) * mm, "end": v(37.83, -3.78) * mm});
            skLineSegment(sketch, "E51.10.20", {"start": v(37.1, -3.86) * mm, "end": v(37.42, -3.83) * mm});
            skLineSegment(sketch, "E51.10.21", {"start": v(38.02, -0.2) * mm, "end": v(38.5, -0.33) * mm});
            skLineSegment(sketch, "E51.10.22", {"start": v(37.62, -0.1) * mm, "end": v(38.02, -0.2) * mm});
            skLineSegment(sketch, "E51.10.23", {"start": v(37.07, -0.01) * mm, "end": v(37.3, -0.04) * mm});
            skLineSegment(sketch, "E51.10.24", {"start": v(36.68, -3.86) * mm, "end": v(36.73, -3.86) * mm});
            skLineSegment(sketch, "E51.10.25", {"start": v(36.73, -3.86) * mm, "end": v(36.87, -3.86) * mm});
            skLineSegment(sketch, "E51.10.26", {"start": v(37.3, -0.04) * mm, "end": v(37.62, -0.1) * mm});
            skLineSegment(sketch, "E51.10.27", {"start": v(36.87, -3.86) * mm, "end": v(37.1, -3.86) * mm});
            skLineSegment(sketch, "E51.10.28", {"start": v(36.93, 0) * mm, "end": v(37.07, -0.01) * mm});
            skLineSegment(sketch, "E51.10.29", {"start": v(36.89, 0) * mm, "end": v(36.93, 0) * mm});
            skLineSegment(sketch, "E51.11.0", {"start": v(33.44, 10.87) * mm, "end": v(35.08, 11.4) * mm});
            skLineSegment(sketch, "E51.11.1", {"start": v(40.72, 10.68) * mm, "end": v(41.47, 11.43) * mm});
            skLineSegment(sketch, "E51.11.2", {"start": v(34.4, 7.31) * mm, "end": v(36.08, 7.67) * mm});
            skLineSegment(sketch, "E51.11.3", {"start": v(40, 10.03) * mm, "end": v(40.72, 10.68) * mm});
            skLineSegment(sketch, "E51.11.4", {"start": v(39.66, 11.31) * mm, "end": v(40.6, 11.1) * mm});
            skLineSegment(sketch, "E51.11.5", {"start": v(40.6, 11.1) * mm, "end": v(41.63, 10.83) * mm});
            skLineSegment(sketch, "E51.11.6", {"start": v(39.32, 9.48) * mm, "end": v(40, 10.03) * mm});
            skLineSegment(sketch, "E51.11.7", {"start": v(42.24, 12.29) * mm, "end": v(43.03, 13.25) * mm});
            skLineSegment(sketch, "E51.11.8", {"start": v(38.7, 9.02) * mm, "end": v(39.32, 9.48) * mm});
            skLineSegment(sketch, "E51.11.9", {"start": v(42.73, 10.48) * mm, "end": v(43.9, 10.04) * mm});
            skLineSegment(sketch, "E51.11.10", {"start": v(41.47, 11.43) * mm, "end": v(42.24, 12.29) * mm});
            skLineSegment(sketch, "E51.11.11", {"start": v(38.8, 11.45) * mm, "end": v(39.66, 11.31) * mm});
            skLineSegment(sketch, "E51.11.12", {"start": v(41.63, 10.83) * mm, "end": v(42.73, 10.48) * mm});
            skLineSegment(sketch, "E51.11.13", {"start": v(37.15, 8.1) * mm, "end": v(37.6, 8.33) * mm});
            skLineSegment(sketch, "E51.11.14", {"start": v(37.6, 8.33) * mm, "end": v(38.11, 8.63) * mm});
            skLineSegment(sketch, "E51.11.15", {"start": v(38.11, 8.63) * mm, "end": v(38.7, 9.02) * mm});
            skLineSegment(sketch, "E51.11.16", {"start": v(37.33, 11.58) * mm, "end": v(38.02, 11.54) * mm});
            skLineSegment(sketch, "E51.11.17", {"start": v(36.73, 11.59) * mm, "end": v(37.33, 11.58) * mm});
            skLineSegment(sketch, "E51.11.18", {"start": v(38.02, 11.54) * mm, "end": v(38.8, 11.45) * mm});
            skLineSegment(sketch, "E51.11.19", {"start": v(36.77, 7.92) * mm, "end": v(37.15, 8.1) * mm});
            skLineSegment(sketch, "E51.11.20", {"start": v(36.48, 7.8) * mm, "end": v(36.77, 7.92) * mm});
            skLineSegment(sketch, "E51.11.21", {"start": v(36.22, 11.57) * mm, "end": v(36.73, 11.59) * mm});
            skLineSegment(sketch, "E51.11.22", {"start": v(35.8, 11.53) * mm, "end": v(36.22, 11.57) * mm});
            skLineSegment(sketch, "E51.11.23", {"start": v(35.26, 11.44) * mm, "end": v(35.49, 11.49) * mm});
            skLineSegment(sketch, "E51.11.24", {"start": v(36.08, 7.67) * mm, "end": v(36.13, 7.68) * mm});
            skLineSegment(sketch, "E51.11.25", {"start": v(36.13, 7.68) * mm, "end": v(36.26, 7.72) * mm});
            skLineSegment(sketch, "E51.11.26", {"start": v(35.49, 11.49) * mm, "end": v(35.8, 11.53) * mm});
            skLineSegment(sketch, "E51.11.27", {"start": v(36.26, 7.72) * mm, "end": v(36.48, 7.8) * mm});
            skLineSegment(sketch, "E51.11.28", {"start": v(35.13, 11.41) * mm, "end": v(35.26, 11.44) * mm});
            skLineSegment(sketch, "E51.11.29", {"start": v(35.08, 11.4) * mm, "end": v(35.13, 11.41) * mm});
            skLineSegment(sketch, "E51.12.0", {"start": v(28.45, 20.67) * mm, "end": v(29.84, 21.68) * mm});
            skLineSegment(sketch, "E51.12.1", {"start": v(35.42, 22.74) * mm, "end": v(35.9, 23.69) * mm});
            skLineSegment(sketch, "E51.12.2", {"start": v(30.45, 17.58) * mm, "end": v(31.94, 18.44) * mm});
            skLineSegment(sketch, "E51.12.3", {"start": v(34.94, 21.9) * mm, "end": v(35.42, 22.74) * mm});
            skLineSegment(sketch, "E51.12.4", {"start": v(34.22, 23.01) * mm, "end": v(35.19, 23.11) * mm});
            skLineSegment(sketch, "E51.12.5", {"start": v(35.19, 23.11) * mm, "end": v(36.24, 23.17) * mm});
            skLineSegment(sketch, "E51.12.6", {"start": v(34.47, 21.17) * mm, "end": v(34.94, 21.9) * mm});
            skLineSegment(sketch, "E51.12.7", {"start": v(36.38, 24.74) * mm, "end": v(36.83, 25.9) * mm});
            skLineSegment(sketch, "E51.12.8", {"start": v(34.01, 20.53) * mm, "end": v(34.47, 21.17) * mm});
            skLineSegment(sketch, "E51.12.9", {"start": v(37.4, 23.17) * mm, "end": v(38.64, 23.11) * mm});
            skLineSegment(sketch, "E51.12.10", {"start": v(35.9, 23.69) * mm, "end": v(36.38, 24.74) * mm});
            skLineSegment(sketch, "E51.12.11", {"start": v(33.36, 22.88) * mm, "end": v(34.22, 23.01) * mm});
            skLineSegment(sketch, "E51.12.12", {"start": v(36.24, 23.17) * mm, "end": v(37.4, 23.17) * mm});
            skLineSegment(sketch, "E51.12.13", {"start": v(32.83, 19.18) * mm, "end": v(33.19, 19.54) * mm});
            skLineSegment(sketch, "E51.12.14", {"start": v(33.19, 19.54) * mm, "end": v(33.58, 19.99) * mm});
            skLineSegment(sketch, "E51.12.15", {"start": v(33.58, 19.99) * mm, "end": v(34.01, 20.53) * mm});
            skLineSegment(sketch, "E51.12.16", {"start": v(31.92, 22.55) * mm, "end": v(32.59, 22.72) * mm});
            skLineSegment(sketch, "E51.12.17", {"start": v(31.35, 22.37) * mm, "end": v(31.92, 22.55) * mm});
            skLineSegment(sketch, "E51.12.18", {"start": v(32.59, 22.72) * mm, "end": v(33.36, 22.88) * mm});
            skLineSegment(sketch, "E51.12.19", {"start": v(32.53, 18.9) * mm, "end": v(32.83, 19.18) * mm});
            skLineSegment(sketch, "E51.12.20", {"start": v(32.28, 18.69) * mm, "end": v(32.53, 18.9) * mm});
            skLineSegment(sketch, "E51.12.21", {"start": v(30.87, 22.2) * mm, "end": v(31.35, 22.37) * mm});
            skLineSegment(sketch, "E51.12.22", {"start": v(30.5, 22.03) * mm, "end": v(30.87, 22.2) * mm});
            skLineSegment(sketch, "E51.12.23", {"start": v(30, 21.78) * mm, "end": v(30.2, 21.9) * mm});
            skLineSegment(sketch, "E51.12.24", {"start": v(31.94, 18.44) * mm, "end": v(31.98, 18.47) * mm});
            skLineSegment(sketch, "E51.12.25", {"start": v(31.98, 18.47) * mm, "end": v(32.1, 18.55) * mm});
            skLineSegment(sketch, "E51.12.26", {"start": v(30.2, 21.9) * mm, "end": v(30.5, 22.03) * mm});
            skLineSegment(sketch, "E51.12.27", {"start": v(32.1, 18.55) * mm, "end": v(32.28, 18.69) * mm});
            skLineSegment(sketch, "E51.12.28", {"start": v(29.88, 21.7) * mm, "end": v(30, 21.78) * mm});
            skLineSegment(sketch, "E51.12.29", {"start": v(29.84, 21.68) * mm, "end": v(29.88, 21.7) * mm});
            skLineSegment(sketch, "E51.13.0", {"start": v(20.67, 28.45) * mm, "end": v(21.68, 29.84) * mm});
            skLineSegment(sketch, "E51.13.1", {"start": v(26.66, 32.58) * mm, "end": v(26.83, 33.62) * mm});
            skLineSegment(sketch, "E51.13.2", {"start": v(23.53, 26.13) * mm, "end": v(24.68, 27.41) * mm});
            skLineSegment(sketch, "E51.13.3", {"start": v(26.46, 31.63) * mm, "end": v(26.66, 32.58) * mm});
            skLineSegment(sketch, "E51.13.4", {"start": v(25.44, 32.46) * mm, "end": v(26.32, 32.85) * mm});
            skLineSegment(sketch, "E51.13.5", {"start": v(26.32, 32.85) * mm, "end": v(27.31, 33.23) * mm});
            skLineSegment(sketch, "E51.13.6", {"start": v(26.24, 30.78) * mm, "end": v(26.46, 31.63) * mm});
            skLineSegment(sketch, "E51.13.7", {"start": v(26.95, 34.77) * mm, "end": v(27.02, 36.01) * mm});
            skLineSegment(sketch, "E51.13.8", {"start": v(26, 30.04) * mm, "end": v(26.24, 30.78) * mm});
            skLineSegment(sketch, "E51.13.9", {"start": v(28.4, 33.6) * mm, "end": v(29.6, 33.92) * mm});
            skLineSegment(sketch, "E51.13.10", {"start": v(26.83, 33.62) * mm, "end": v(26.95, 34.77) * mm});
            skLineSegment(sketch, "E51.13.11", {"start": v(24.65, 32.07) * mm, "end": v(25.44, 32.46) * mm});
            skLineSegment(sketch, "E51.13.12", {"start": v(27.31, 33.23) * mm, "end": v(28.4, 33.6) * mm});
            skLineSegment(sketch, "E51.13.13", {"start": v(25.3, 28.38) * mm, "end": v(25.52, 28.84) * mm});
            skLineSegment(sketch, "E51.13.14", {"start": v(25.52, 28.84) * mm, "end": v(25.76, 29.39) * mm});
            skLineSegment(sketch, "E51.13.15", {"start": v(25.76, 29.39) * mm, "end": v(26, 30.04) * mm});
            skLineSegment(sketch, "E51.13.16", {"start": v(23.4, 31.3) * mm, "end": v(23.97, 31.68) * mm});
            skLineSegment(sketch, "E51.13.17", {"start": v(22.9, 30.96) * mm, "end": v(23.4, 31.3) * mm});
            skLineSegment(sketch, "E51.13.18", {"start": v(23.97, 31.68) * mm, "end": v(24.65, 32.07) * mm});
            skLineSegment(sketch, "E51.13.19", {"start": v(25.1, 28.02) * mm, "end": v(25.3, 28.38) * mm});
            skLineSegment(sketch, "E51.13.20", {"start": v(24.93, 27.75) * mm, "end": v(25.1, 28.02) * mm});
            skLineSegment(sketch, "E51.13.21", {"start": v(22.5, 30.65) * mm, "end": v(22.9, 30.96) * mm});
            skLineSegment(sketch, "E51.13.22", {"start": v(22.19, 30.38) * mm, "end": v(22.5, 30.65) * mm});
            skLineSegment(sketch, "E51.13.23", {"start": v(21.8, 29.98) * mm, "end": v(21.96, 30.15) * mm});
            skLineSegment(sketch, "E51.13.24", {"start": v(24.68, 27.41) * mm, "end": v(24.71, 27.45) * mm});
            skLineSegment(sketch, "E51.13.25", {"start": v(24.71, 27.45) * mm, "end": v(24.8, 27.56) * mm});
            skLineSegment(sketch, "E51.13.26", {"start": v(21.96, 30.15) * mm, "end": v(22.19, 30.38) * mm});
            skLineSegment(sketch, "E51.13.27", {"start": v(24.8, 27.56) * mm, "end": v(24.93, 27.75) * mm});
            skLineSegment(sketch, "E51.13.28", {"start": v(21.7, 29.88) * mm, "end": v(21.8, 29.98) * mm});
            skLineSegment(sketch, "E51.13.29", {"start": v(21.68, 29.84) * mm, "end": v(21.7, 29.88) * mm});
            skLineSegment(sketch, "E51.14.0", {"start": v(10.87, 33.44) * mm, "end": v(11.4, 35.08) * mm});
            skLineSegment(sketch, "E51.14.1", {"start": v(15.3, 39.22) * mm, "end": v(15.13, 40.27) * mm});
            skLineSegment(sketch, "E51.14.2", {"start": v(14.3, 32.12) * mm, "end": v(15, 33.7) * mm});
            skLineSegment(sketch, "E51.14.3", {"start": v(15.4, 38.26) * mm, "end": v(15.3, 39.22) * mm});
            skLineSegment(sketch, "E51.14.4", {"start": v(14.16, 38.73) * mm, "end": v(14.88, 39.38) * mm});
            skLineSegment(sketch, "E51.14.5", {"start": v(14.88, 39.38) * mm, "end": v(15.7, 40.05) * mm});
            skLineSegment(sketch, "E51.14.6", {"start": v(15.44, 37.39) * mm, "end": v(15.4, 38.26) * mm});
            skLineSegment(sketch, "E51.14.7", {"start": v(14.89, 41.4) * mm, "end": v(14.57, 42.6) * mm});
            skLineSegment(sketch, "E51.14.8", {"start": v(15.45, 36.6) * mm, "end": v(15.44, 37.39) * mm});
            skLineSegment(sketch, "E51.14.9", {"start": v(16.64, 40.73) * mm, "end": v(17.68, 41.41) * mm});
            skLineSegment(sketch, "E51.14.10", {"start": v(15.13, 40.27) * mm, "end": v(14.89, 41.4) * mm});
            skLineSegment(sketch, "E51.14.11", {"start": v(13.54, 38.12) * mm, "end": v(14.16, 38.73) * mm});
            skLineSegment(sketch, "E51.14.12", {"start": v(15.7, 40.05) * mm, "end": v(16.64, 40.73) * mm});
            skLineSegment(sketch, "E51.14.13", {"start": v(15.3, 34.81) * mm, "end": v(15.36, 35.31) * mm});
            skLineSegment(sketch, "E51.14.14", {"start": v(15.36, 35.31) * mm, "end": v(15.42, 35.91) * mm});
            skLineSegment(sketch, "E51.14.15", {"start": v(15.42, 35.91) * mm, "end": v(15.45, 36.6) * mm});
            skLineSegment(sketch, "E51.14.16", {"start": v(12.57, 37) * mm, "end": v(13.01, 37.54) * mm});
            skLineSegment(sketch, "E51.14.17", {"start": v(12.21, 36.52) * mm, "end": v(12.57, 37) * mm});
            skLineSegment(sketch, "E51.14.18", {"start": v(13.01, 37.54) * mm, "end": v(13.54, 38.12) * mm});
            skLineSegment(sketch, "E51.14.19", {"start": v(15.21, 34.4) * mm, "end": v(15.3, 34.81) * mm});
            skLineSegment(sketch, "E51.14.20", {"start": v(15.13, 34.1) * mm, "end": v(15.21, 34.4) * mm});
            skLineSegment(sketch, "E51.14.21", {"start": v(11.93, 36.1) * mm, "end": v(12.21, 36.52) * mm});
            skLineSegment(sketch, "E51.14.22", {"start": v(11.72, 35.75) * mm, "end": v(11.93, 36.1) * mm});
            skLineSegment(sketch, "E51.14.23", {"start": v(11.47, 35.25) * mm, "end": v(11.57, 35.46) * mm});
            skLineSegment(sketch, "E51.14.24", {"start": v(15, 33.7) * mm, "end": v(15.02, 33.74) * mm});
            skLineSegment(sketch, "E51.14.25", {"start": v(15.02, 33.74) * mm, "end": v(15.07, 33.87) * mm});
            skLineSegment(sketch, "E51.14.26", {"start": v(11.57, 35.46) * mm, "end": v(11.72, 35.75) * mm});
            skLineSegment(sketch, "E51.14.27", {"start": v(15.07, 33.87) * mm, "end": v(15.13, 34.1) * mm});
            skLineSegment(sketch, "E51.14.28", {"start": v(11.41, 35.12) * mm, "end": v(11.47, 35.25) * mm});
            skLineSegment(sketch, "E51.14.29", {"start": v(11.4, 35.08) * mm, "end": v(11.41, 35.12) * mm});
            skLineSegment(sketch, "E51.15.0", {"start": v(0, 35.16) * mm, "end": v(0, 36.89) * mm});
            skLineSegment(sketch, "E51.15.1", {"start": v(2.42, 42.03) * mm, "end": v(1.94, 42.97) * mm});
            skLineSegment(sketch, "E51.15.2", {"start": v(3.68, 34.97) * mm, "end": v(3.86, 36.68) * mm});
            skLineSegment(sketch, "E51.15.3", {"start": v(2.82, 41.14) * mm, "end": v(2.42, 42.03) * mm});
            skLineSegment(sketch, "E51.15.4", {"start": v(1.5, 41.21) * mm, "end": v(1.98, 42.05) * mm});
            skLineSegment(sketch, "E51.15.5", {"start": v(1.98, 42.05) * mm, "end": v(2.56, 42.94) * mm});
            skLineSegment(sketch, "E51.15.6", {"start": v(3.13, 40.33) * mm, "end": v(2.82, 41.14) * mm});
            skLineSegment(sketch, "E51.15.7", {"start": v(1.37, 43.97) * mm, "end": v(0.7, 45.02) * mm});
            skLineSegment(sketch, "E51.15.8", {"start": v(3.38, 39.58) * mm, "end": v(3.13, 40.33) * mm});
            skLineSegment(sketch, "E51.15.9", {"start": v(3.24, 43.87) * mm, "end": v(4.01, 44.85) * mm});
            skLineSegment(sketch, "E51.15.10", {"start": v(1.94, 42.97) * mm, "end": v(1.37, 43.97) * mm});
            skLineSegment(sketch, "E51.15.11", {"start": v(1.1, 40.43) * mm, "end": v(1.5, 41.21) * mm});
            skLineSegment(sketch, "E51.15.12", {"start": v(2.56, 42.94) * mm, "end": v(3.24, 43.87) * mm});
            skLineSegment(sketch, "E51.15.13", {"start": v(3.78, 37.83) * mm, "end": v(3.7, 38.33) * mm});
            skLineSegment(sketch, "E51.15.14", {"start": v(3.7, 38.33) * mm, "end": v(3.57, 38.92) * mm});
            skLineSegment(sketch, "E51.15.15", {"start": v(3.57, 38.92) * mm, "end": v(3.38, 39.58) * mm});
            skLineSegment(sketch, "E51.15.16", {"start": v(0.52, 39.08) * mm, "end": v(0.77, 39.72) * mm});
            skLineSegment(sketch, "E51.15.17", {"start": v(0.33, 38.5) * mm, "end": v(0.52, 39.08) * mm});
            skLineSegment(sketch, "E51.15.18", {"start": v(0.77, 39.72) * mm, "end": v(1.1, 40.43) * mm});
            skLineSegment(sketch, "E51.15.19", {"start": v(3.83, 37.42) * mm, "end": v(3.78, 37.83) * mm});
            skLineSegment(sketch, "E51.15.20", {"start": v(3.86, 37.1) * mm, "end": v(3.83, 37.42) * mm});
            skLineSegment(sketch, "E51.15.21", {"start": v(0.2, 38.02) * mm, "end": v(0.33, 38.5) * mm});
            skLineSegment(sketch, "E51.15.22", {"start": v(0.1, 37.62) * mm, "end": v(0.2, 38.02) * mm});
            skLineSegment(sketch, "E51.15.23", {"start": v(0.01, 37.07) * mm, "end": v(0.04, 37.3) * mm});
            skLineSegment(sketch, "E51.15.24", {"start": v(3.86, 36.68) * mm, "end": v(3.86, 36.73) * mm});
            skLineSegment(sketch, "E51.15.25", {"start": v(3.86, 36.73) * mm, "end": v(3.86, 36.87) * mm});
            skLineSegment(sketch, "E51.15.26", {"start": v(0.04, 37.3) * mm, "end": v(0.1, 37.62) * mm});
            skLineSegment(sketch, "E51.15.27", {"start": v(3.86, 36.87) * mm, "end": v(3.86, 37.1) * mm});
            skLineSegment(sketch, "E51.15.28", {"start": v(0, 36.93) * mm, "end": v(0.01, 37.07) * mm});
            skLineSegment(sketch, "E51.15.29", {"start": v(0, 36.89) * mm, "end": v(0, 36.93) * mm});
            skLineSegment(sketch, "E51.16.0", {"start": v(-10.87, 33.44) * mm, "end": v(-11.4, 35.08) * mm});
            skLineSegment(sketch, "E51.16.1", {"start": v(-10.68, 40.72) * mm, "end": v(-11.43, 41.47) * mm});
            skLineSegment(sketch, "E51.16.2", {"start": v(-7.31, 34.4) * mm, "end": v(-7.67, 36.08) * mm});
            skLineSegment(sketch, "E51.16.3", {"start": v(-10.03, 40) * mm, "end": v(-10.68, 40.72) * mm});
            skLineSegment(sketch, "E51.16.4", {"start": v(-11.31, 39.66) * mm, "end": v(-11.1, 40.6) * mm});
            skLineSegment(sketch, "E51.16.5", {"start": v(-11.1, 40.6) * mm, "end": v(-10.83, 41.63) * mm});
            skLineSegment(sketch, "E51.16.6", {"start": v(-9.48, 39.32) * mm, "end": v(-10.03, 40) * mm});
            skLineSegment(sketch, "E51.16.7", {"start": v(-12.29, 42.24) * mm, "end": v(-13.25, 43.03) * mm});
            skLineSegment(sketch, "E51.16.8", {"start": v(-9.02, 38.7) * mm, "end": v(-9.48, 39.32) * mm});
            skLineSegment(sketch, "E51.16.9", {"start": v(-10.48, 42.73) * mm, "end": v(-10.04, 43.9) * mm});
            skLineSegment(sketch, "E51.16.10", {"start": v(-11.43, 41.47) * mm, "end": v(-12.29, 42.24) * mm});
            skLineSegment(sketch, "E51.16.11", {"start": v(-11.45, 38.8) * mm, "end": v(-11.31, 39.66) * mm});
            skLineSegment(sketch, "E51.16.12", {"start": v(-10.83, 41.63) * mm, "end": v(-10.48, 42.73) * mm});
            skLineSegment(sketch, "E51.16.13", {"start": v(-8.1, 37.15) * mm, "end": v(-8.33, 37.6) * mm});
            skLineSegment(sketch, "E51.16.14", {"start": v(-8.33, 37.6) * mm, "end": v(-8.63, 38.11) * mm});
            skLineSegment(sketch, "E51.16.15", {"start": v(-8.63, 38.11) * mm, "end": v(-9.02, 38.7) * mm});
            skLineSegment(sketch, "E51.16.16", {"start": v(-11.58, 37.33) * mm, "end": v(-11.54, 38.02) * mm});
            skLineSegment(sketch, "E51.16.17", {"start": v(-11.59, 36.73) * mm, "end": v(-11.58, 37.33) * mm});
            skLineSegment(sketch, "E51.16.18", {"start": v(-11.54, 38.02) * mm, "end": v(-11.45, 38.8) * mm});
            skLineSegment(sketch, "E51.16.19", {"start": v(-7.92, 36.77) * mm, "end": v(-8.1, 37.15) * mm});
            skLineSegment(sketch, "E51.16.20", {"start": v(-7.8, 36.48) * mm, "end": v(-7.92, 36.77) * mm});
            skLineSegment(sketch, "E51.16.21", {"start": v(-11.57, 36.22) * mm, "end": v(-11.59, 36.73) * mm});
            skLineSegment(sketch, "E51.16.22", {"start": v(-11.53, 35.8) * mm, "end": v(-11.57, 36.22) * mm});
            skLineSegment(sketch, "E51.16.23", {"start": v(-11.44, 35.26) * mm, "end": v(-11.49, 35.49) * mm});
            skLineSegment(sketch, "E51.16.24", {"start": v(-7.67, 36.08) * mm, "end": v(-7.68, 36.13) * mm});
            skLineSegment(sketch, "E51.16.25", {"start": v(-7.68, 36.13) * mm, "end": v(-7.72, 36.26) * mm});
            skLineSegment(sketch, "E51.16.26", {"start": v(-11.49, 35.49) * mm, "end": v(-11.53, 35.8) * mm});
            skLineSegment(sketch, "E51.16.27", {"start": v(-7.72, 36.26) * mm, "end": v(-7.8, 36.48) * mm});
            skLineSegment(sketch, "E51.16.28", {"start": v(-11.41, 35.13) * mm, "end": v(-11.44, 35.26) * mm});
            skLineSegment(sketch, "E51.16.29", {"start": v(-11.4, 35.08) * mm, "end": v(-11.41, 35.13) * mm});
            skLineSegment(sketch, "E51.17.0", {"start": v(-20.67, 28.45) * mm, "end": v(-21.68, 29.84) * mm});
            skLineSegment(sketch, "E51.17.1", {"start": v(-22.74, 35.42) * mm, "end": v(-23.69, 35.9) * mm});
            skLineSegment(sketch, "E51.17.2", {"start": v(-17.58, 30.45) * mm, "end": v(-18.44, 31.94) * mm});
            skLineSegment(sketch, "E51.17.3", {"start": v(-21.9, 34.94) * mm, "end": v(-22.74, 35.42) * mm});
            skLineSegment(sketch, "E51.17.4", {"start": v(-23.01, 34.22) * mm, "end": v(-23.11, 35.19) * mm});
            skLineSegment(sketch, "E51.17.5", {"start": v(-23.11, 35.19) * mm, "end": v(-23.17, 36.24) * mm});
            skLineSegment(sketch, "E51.17.6", {"start": v(-21.17, 34.47) * mm, "end": v(-21.9, 34.94) * mm});
            skLineSegment(sketch, "E51.17.7", {"start": v(-24.74, 36.38) * mm, "end": v(-25.9, 36.83) * mm});
            skLineSegment(sketch, "E51.17.8", {"start": v(-20.53, 34.01) * mm, "end": v(-21.17, 34.47) * mm});
            skLineSegment(sketch, "E51.17.9", {"start": v(-23.17, 37.4) * mm, "end": v(-23.11, 38.64) * mm});
            skLineSegment(sketch, "E51.17.10", {"start": v(-23.69, 35.9) * mm, "end": v(-24.74, 36.38) * mm});
            skLineSegment(sketch, "E51.17.11", {"start": v(-22.88, 33.36) * mm, "end": v(-23.01, 34.22) * mm});
            skLineSegment(sketch, "E51.17.12", {"start": v(-23.17, 36.24) * mm, "end": v(-23.17, 37.4) * mm});
            skLineSegment(sketch, "E51.17.13", {"start": v(-19.18, 32.83) * mm, "end": v(-19.54, 33.19) * mm});
            skLineSegment(sketch, "E51.17.14", {"start": v(-19.54, 33.19) * mm, "end": v(-19.99, 33.58) * mm});
            skLineSegment(sketch, "E51.17.15", {"start": v(-19.99, 33.58) * mm, "end": v(-20.53, 34.01) * mm});
            skLineSegment(sketch, "E51.17.16", {"start": v(-22.55, 31.92) * mm, "end": v(-22.72, 32.59) * mm});
            skLineSegment(sketch, "E51.17.17", {"start": v(-22.37, 31.35) * mm, "end": v(-22.55, 31.92) * mm});
            skLineSegment(sketch, "E51.17.18", {"start": v(-22.72, 32.59) * mm, "end": v(-22.88, 33.36) * mm});
            skLineSegment(sketch, "E51.17.19", {"start": v(-18.9, 32.53) * mm, "end": v(-19.18, 32.83) * mm});
            skLineSegment(sketch, "E51.17.20", {"start": v(-18.69, 32.28) * mm, "end": v(-18.9, 32.53) * mm});
            skLineSegment(sketch, "E51.17.21", {"start": v(-22.2, 30.87) * mm, "end": v(-22.37, 31.35) * mm});
            skLineSegment(sketch, "E51.17.22", {"start": v(-22.03, 30.5) * mm, "end": v(-22.2, 30.87) * mm});
            skLineSegment(sketch, "E51.17.23", {"start": v(-21.78, 30) * mm, "end": v(-21.9, 30.2) * mm});
            skLineSegment(sketch, "E51.17.24", {"start": v(-18.44, 31.94) * mm, "end": v(-18.47, 31.98) * mm});
            skLineSegment(sketch, "E51.17.25", {"start": v(-18.47, 31.98) * mm, "end": v(-18.55, 32.1) * mm});
            skLineSegment(sketch, "E51.17.26", {"start": v(-21.9, 30.2) * mm, "end": v(-22.03, 30.5) * mm});
            skLineSegment(sketch, "E51.17.27", {"start": v(-18.55, 32.1) * mm, "end": v(-18.69, 32.28) * mm});
            skLineSegment(sketch, "E51.17.28", {"start": v(-21.7, 29.88) * mm, "end": v(-21.78, 30) * mm});
            skLineSegment(sketch, "E51.17.29", {"start": v(-21.68, 29.84) * mm, "end": v(-21.7, 29.88) * mm});
            skLineSegment(sketch, "E51.18.0", {"start": v(-28.45, 20.67) * mm, "end": v(-29.84, 21.68) * mm});
            skLineSegment(sketch, "E51.18.1", {"start": v(-32.58, 26.66) * mm, "end": v(-33.62, 26.83) * mm});
            skLineSegment(sketch, "E51.18.2", {"start": v(-26.13, 23.53) * mm, "end": v(-27.41, 24.68) * mm});
            skLineSegment(sketch, "E51.18.3", {"start": v(-31.63, 26.46) * mm, "end": v(-32.58, 26.66) * mm});
            skLineSegment(sketch, "E51.18.4", {"start": v(-32.46, 25.44) * mm, "end": v(-32.85, 26.32) * mm});
            skLineSegment(sketch, "E51.18.5", {"start": v(-32.85, 26.32) * mm, "end": v(-33.23, 27.31) * mm});
            skLineSegment(sketch, "E51.18.6", {"start": v(-30.78, 26.24) * mm, "end": v(-31.63, 26.46) * mm});
            skLineSegment(sketch, "E51.18.7", {"start": v(-34.77, 26.95) * mm, "end": v(-36.01, 27.02) * mm});
            skLineSegment(sketch, "E51.18.8", {"start": v(-30.04, 26) * mm, "end": v(-30.78, 26.24) * mm});
            skLineSegment(sketch, "E51.18.9", {"start": v(-33.6, 28.4) * mm, "end": v(-33.92, 29.6) * mm});
            skLineSegment(sketch, "E51.18.10", {"start": v(-33.62, 26.83) * mm, "end": v(-34.77, 26.95) * mm});
            skLineSegment(sketch, "E51.18.11", {"start": v(-32.07, 24.65) * mm, "end": v(-32.46, 25.44) * mm});
            skLineSegment(sketch, "E51.18.12", {"start": v(-33.23, 27.31) * mm, "end": v(-33.6, 28.4) * mm});
            skLineSegment(sketch, "E51.18.13", {"start": v(-28.38, 25.3) * mm, "end": v(-28.84, 25.52) * mm});
            skLineSegment(sketch, "E51.18.14", {"start": v(-28.84, 25.52) * mm, "end": v(-29.39, 25.76) * mm});
            skLineSegment(sketch, "E51.18.15", {"start": v(-29.39, 25.76) * mm, "end": v(-30.04, 26) * mm});
            skLineSegment(sketch, "E51.18.16", {"start": v(-31.3, 23.4) * mm, "end": v(-31.68, 23.97) * mm});
            skLineSegment(sketch, "E51.18.17", {"start": v(-30.96, 22.9) * mm, "end": v(-31.3, 23.4) * mm});
            skLineSegment(sketch, "E51.18.18", {"start": v(-31.68, 23.97) * mm, "end": v(-32.07, 24.65) * mm});
            skLineSegment(sketch, "E51.18.19", {"start": v(-28.02, 25.1) * mm, "end": v(-28.38, 25.3) * mm});
            skLineSegment(sketch, "E51.18.20", {"start": v(-27.75, 24.93) * mm, "end": v(-28.02, 25.1) * mm});
            skLineSegment(sketch, "E51.18.21", {"start": v(-30.65, 22.5) * mm, "end": v(-30.96, 22.9) * mm});
            skLineSegment(sketch, "E51.18.22", {"start": v(-30.38, 22.19) * mm, "end": v(-30.65, 22.5) * mm});
            skLineSegment(sketch, "E51.18.23", {"start": v(-29.98, 21.8) * mm, "end": v(-30.15, 21.96) * mm});
            skLineSegment(sketch, "E51.18.24", {"start": v(-27.41, 24.68) * mm, "end": v(-27.45, 24.71) * mm});
            skLineSegment(sketch, "E51.18.25", {"start": v(-27.45, 24.71) * mm, "end": v(-27.56, 24.8) * mm});
            skLineSegment(sketch, "E51.18.26", {"start": v(-30.15, 21.96) * mm, "end": v(-30.38, 22.19) * mm});
            skLineSegment(sketch, "E51.18.27", {"start": v(-27.56, 24.8) * mm, "end": v(-27.75, 24.93) * mm});
            skLineSegment(sketch, "E51.18.28", {"start": v(-29.88, 21.7) * mm, "end": v(-29.98, 21.8) * mm});
            skLineSegment(sketch, "E51.18.29", {"start": v(-29.84, 21.68) * mm, "end": v(-29.88, 21.7) * mm});
            skLineSegment(sketch, "E51.19.0", {"start": v(-33.44, 10.87) * mm, "end": v(-35.08, 11.4) * mm});
            skLineSegment(sketch, "E51.19.1", {"start": v(-39.22, 15.3) * mm, "end": v(-40.27, 15.13) * mm});
            skLineSegment(sketch, "E51.19.2", {"start": v(-32.12, 14.3) * mm, "end": v(-33.7, 15) * mm});
            skLineSegment(sketch, "E51.19.3", {"start": v(-38.26, 15.4) * mm, "end": v(-39.22, 15.3) * mm});
            skLineSegment(sketch, "E51.19.4", {"start": v(-38.73, 14.16) * mm, "end": v(-39.38, 14.88) * mm});
            skLineSegment(sketch, "E51.19.5", {"start": v(-39.38, 14.88) * mm, "end": v(-40.05, 15.7) * mm});
            skLineSegment(sketch, "E51.19.6", {"start": v(-37.39, 15.44) * mm, "end": v(-38.26, 15.4) * mm});
            skLineSegment(sketch, "E51.19.7", {"start": v(-41.4, 14.89) * mm, "end": v(-42.6, 14.57) * mm});
            skLineSegment(sketch, "E51.19.8", {"start": v(-36.6, 15.45) * mm, "end": v(-37.39, 15.44) * mm});
            skLineSegment(sketch, "E51.19.9", {"start": v(-40.73, 16.64) * mm, "end": v(-41.41, 17.68) * mm});
            skLineSegment(sketch, "E51.19.10", {"start": v(-40.27, 15.13) * mm, "end": v(-41.4, 14.89) * mm});
            skLineSegment(sketch, "E51.19.11", {"start": v(-38.12, 13.54) * mm, "end": v(-38.73, 14.16) * mm});
            skLineSegment(sketch, "E51.19.12", {"start": v(-40.05, 15.7) * mm, "end": v(-40.73, 16.64) * mm});
            skLineSegment(sketch, "E51.19.13", {"start": v(-34.81, 15.3) * mm, "end": v(-35.31, 15.36) * mm});
            skLineSegment(sketch, "E51.19.14", {"start": v(-35.31, 15.36) * mm, "end": v(-35.91, 15.42) * mm});
            skLineSegment(sketch, "E51.19.15", {"start": v(-35.91, 15.42) * mm, "end": v(-36.6, 15.45) * mm});
            skLineSegment(sketch, "E51.19.16", {"start": v(-37, 12.57) * mm, "end": v(-37.54, 13.01) * mm});
            skLineSegment(sketch, "E51.19.17", {"start": v(-36.52, 12.21) * mm, "end": v(-37, 12.57) * mm});
            skLineSegment(sketch, "E51.19.18", {"start": v(-37.54, 13.01) * mm, "end": v(-38.12, 13.54) * mm});
            skLineSegment(sketch, "E51.19.19", {"start": v(-34.4, 15.21) * mm, "end": v(-34.81, 15.3) * mm});
            skLineSegment(sketch, "E51.19.20", {"start": v(-34.1, 15.13) * mm, "end": v(-34.4, 15.21) * mm});
            skLineSegment(sketch, "E51.19.21", {"start": v(-36.1, 11.93) * mm, "end": v(-36.52, 12.21) * mm});
            skLineSegment(sketch, "E51.19.22", {"start": v(-35.75, 11.72) * mm, "end": v(-36.1, 11.93) * mm});
            skLineSegment(sketch, "E51.19.23", {"start": v(-35.25, 11.47) * mm, "end": v(-35.46, 11.57) * mm});
            skLineSegment(sketch, "E51.19.24", {"start": v(-33.7, 15) * mm, "end": v(-33.74, 15.02) * mm});
            skLineSegment(sketch, "E51.19.25", {"start": v(-33.74, 15.02) * mm, "end": v(-33.87, 15.07) * mm});
            skLineSegment(sketch, "E51.19.26", {"start": v(-35.46, 11.57) * mm, "end": v(-35.75, 11.72) * mm});
            skLineSegment(sketch, "E51.19.27", {"start": v(-33.87, 15.07) * mm, "end": v(-34.1, 15.13) * mm});
            skLineSegment(sketch, "E51.19.28", {"start": v(-35.12, 11.41) * mm, "end": v(-35.25, 11.47) * mm});
            skLineSegment(sketch, "E51.19.29", {"start": v(-35.08, 11.4) * mm, "end": v(-35.12, 11.41) * mm});
            skSolve(sketch);
        }
        {
            var Q0;
            {var subQ0=sQuery(id+"F1.wireOp",EDGE,"E0");var subQ27=makeQuery(id+"F1.imprint","INTERSECT",VERTEX,{"derivedFrom":[subQ0,sQuery(id+"F1.wireOp",EDGE,"E51.10.0")]});Q0=makeQuery(id+"F1.imprint","IMPRINT",FACE,{"disambiguationData":[TD([[makeQuery(id+"F1.imprint","IMPRINT",EDGE,{"disambiguationData":[TD([[subQ27,-1.0]])],"derivedFrom":subQ0}),1.0]])]});}
            var Q1;
            {var subQ0=sQuery(id+"F1.wireOp",EDGE,"E51.1.0");Q1=makeQuery(id+"F1.imprint","IMPRINT",FACE,{"disambiguationData":[TD([[makeQuery(id+"F1.imprint","IMPRINT",EDGE,{"derivedFrom":subQ0}),-1.0]])]});}
            var Q2;
            {var subQ7=sQuery(id+"F1.wireOp",EDGE,"E51.2.0");Q2=makeQuery(id+"F1.imprint","IMPRINT",FACE,{"disambiguationData":[TD([[makeQuery(id+"F1.imprint","IMPRINT",EDGE,{"derivedFrom":subQ7}),-1.0]])]});}
            var Q3;
            {var subQ8=sQuery(id+"F1.wireOp",EDGE,"E51.3.0");Q3=makeQuery(id+"F1.imprint","IMPRINT",FACE,{"disambiguationData":[TD([[makeQuery(id+"F1.imprint","IMPRINT",EDGE,{"derivedFrom":subQ8}),-1.0]])]});}
            var Q4;
            {var subQ2=sQuery(id+"F1.wireOp",EDGE,"E51.4.0");Q4=makeQuery(id+"F1.imprint","IMPRINT",FACE,{"disambiguationData":[TD([[makeQuery(id+"F1.imprint","IMPRINT",EDGE,{"derivedFrom":subQ2}),-1.0]])]});}
            var Q5;
            {var subQ8=sQuery(id+"F1.wireOp",EDGE,"E51.5.0");Q5=makeQuery(id+"F1.imprint","IMPRINT",FACE,{"disambiguationData":[TD([[makeQuery(id+"F1.imprint","IMPRINT",EDGE,{"derivedFrom":subQ8}),-1.0]])]});}
            var Q6;
            {var subQ3=sQuery(id+"F1.wireOp",EDGE,"E51.6.0");Q6=makeQuery(id+"F1.imprint","IMPRINT",FACE,{"disambiguationData":[TD([[makeQuery(id+"F1.imprint","IMPRINT",EDGE,{"derivedFrom":subQ3}),-1.0]])]});}
            var Q7;
            {var subQ0=sQuery(id+"F1.wireOp",EDGE,"E51.7.0");Q7=makeQuery(id+"F1.imprint","IMPRINT",FACE,{"disambiguationData":[TD([[makeQuery(id+"F1.imprint","IMPRINT",EDGE,{"derivedFrom":subQ0}),-1.0]])]});}
            var Q8;
            {var subQ5=sQuery(id+"F1.wireOp",EDGE,"E51.8.0");Q8=makeQuery(id+"F1.imprint","IMPRINT",FACE,{"disambiguationData":[TD([[makeQuery(id+"F1.imprint","IMPRINT",EDGE,{"derivedFrom":subQ5}),-1.0]])]});}
            var Q9;
            {var subQ1=sQuery(id+"F1.wireOp",EDGE,"E51.9.0");Q9=makeQuery(id+"F1.imprint","IMPRINT",FACE,{"disambiguationData":[TD([[makeQuery(id+"F1.imprint","IMPRINT",EDGE,{"derivedFrom":subQ1}),-1.0]])]});}
            var Q10;
            {var subQ5=sQuery(id+"F1.wireOp",EDGE,"E51.10.0");Q10=makeQuery(id+"F1.imprint","IMPRINT",FACE,{"disambiguationData":[TD([[makeQuery(id+"F1.imprint","IMPRINT",EDGE,{"derivedFrom":subQ5}),-1.0]])]});}
            var Q11;
            {var subQ8=sQuery(id+"F1.wireOp",EDGE,"E51.11.0");Q11=makeQuery(id+"F1.imprint","IMPRINT",FACE,{"disambiguationData":[TD([[makeQuery(id+"F1.imprint","IMPRINT",EDGE,{"derivedFrom":subQ8}),-1.0]])]});}
            var Q12;
            {var subQ2=sQuery(id+"F1.wireOp",EDGE,"E51.12.0");Q12=makeQuery(id+"F1.imprint","IMPRINT",FACE,{"disambiguationData":[TD([[makeQuery(id+"F1.imprint","IMPRINT",EDGE,{"derivedFrom":subQ2}),-1.0]])]});}
            var Q13;
            {var subQ3=sQuery(id+"F1.wireOp",EDGE,"E51.13.0");Q13=makeQuery(id+"F1.imprint","IMPRINT",FACE,{"disambiguationData":[TD([[makeQuery(id+"F1.imprint","IMPRINT",EDGE,{"derivedFrom":subQ3}),-1.0]])]});}
            var Q14;
            {var subQ0=sQuery(id+"F1.wireOp",EDGE,"E51.14.0");Q14=makeQuery(id+"F1.imprint","IMPRINT",FACE,{"disambiguationData":[TD([[makeQuery(id+"F1.imprint","IMPRINT",EDGE,{"derivedFrom":subQ0}),-1.0]])]});}
            var Q15;
            {var subQ6=sQuery(id+"F1.wireOp",EDGE,"E51.15.0");Q15=makeQuery(id+"F1.imprint","IMPRINT",FACE,{"disambiguationData":[TD([[makeQuery(id+"F1.imprint","IMPRINT",EDGE,{"derivedFrom":subQ6}),-1.0]])]});}
            var Q16;
            {var subQ5=sQuery(id+"F1.wireOp",EDGE,"E51.16.0");Q16=makeQuery(id+"F1.imprint","IMPRINT",FACE,{"disambiguationData":[TD([[makeQuery(id+"F1.imprint","IMPRINT",EDGE,{"derivedFrom":subQ5}),-1.0]])]});}
            var Q17;
            {var subQ7=sQuery(id+"F1.wireOp",EDGE,"E51.17.0");Q17=makeQuery(id+"F1.imprint","IMPRINT",FACE,{"disambiguationData":[TD([[makeQuery(id+"F1.imprint","IMPRINT",EDGE,{"derivedFrom":subQ7}),-1.0]])]});}
            var Q18;
            {var subQ5=sQuery(id+"F1.wireOp",EDGE,"E51.18.0");Q18=makeQuery(id+"F1.imprint","IMPRINT",FACE,{"disambiguationData":[TD([[makeQuery(id+"F1.imprint","IMPRINT",EDGE,{"derivedFrom":subQ5}),-1.0]])]});}
            var Q19;
            {var subQ8=sQuery(id+"F1.wireOp",EDGE,"E51.19.0");Q19=makeQuery(id+"F1.imprint","IMPRINT",FACE,{"disambiguationData":[TD([[makeQuery(id+"F1.imprint","IMPRINT",EDGE,{"derivedFrom":subQ8}),-1.0]])]});}
            var Q20;
            {var subQ8=sQuery(id+"F1.wireOp",EDGE,"E21");Q20=makeQuery(id+"F1.imprint","IMPRINT",FACE,{"disambiguationData":[TD([[makeQuery(id+"F1.imprint","IMPRINT",EDGE,{"derivedFrom":subQ8}),-1.0]])]});}
            extrude(context, id + "F2", {"entities" : qUnion([Q0, Q1, Q2, Q3, Q4, Q5, Q6, Q7, Q8, Q9, Q10, Q11, Q12, Q13, Q14, Q15, Q16, Q17, Q18, Q19, Q20]), "depth" : (getVariable(context, 'GearThickness')) * mm});
        }
    });
